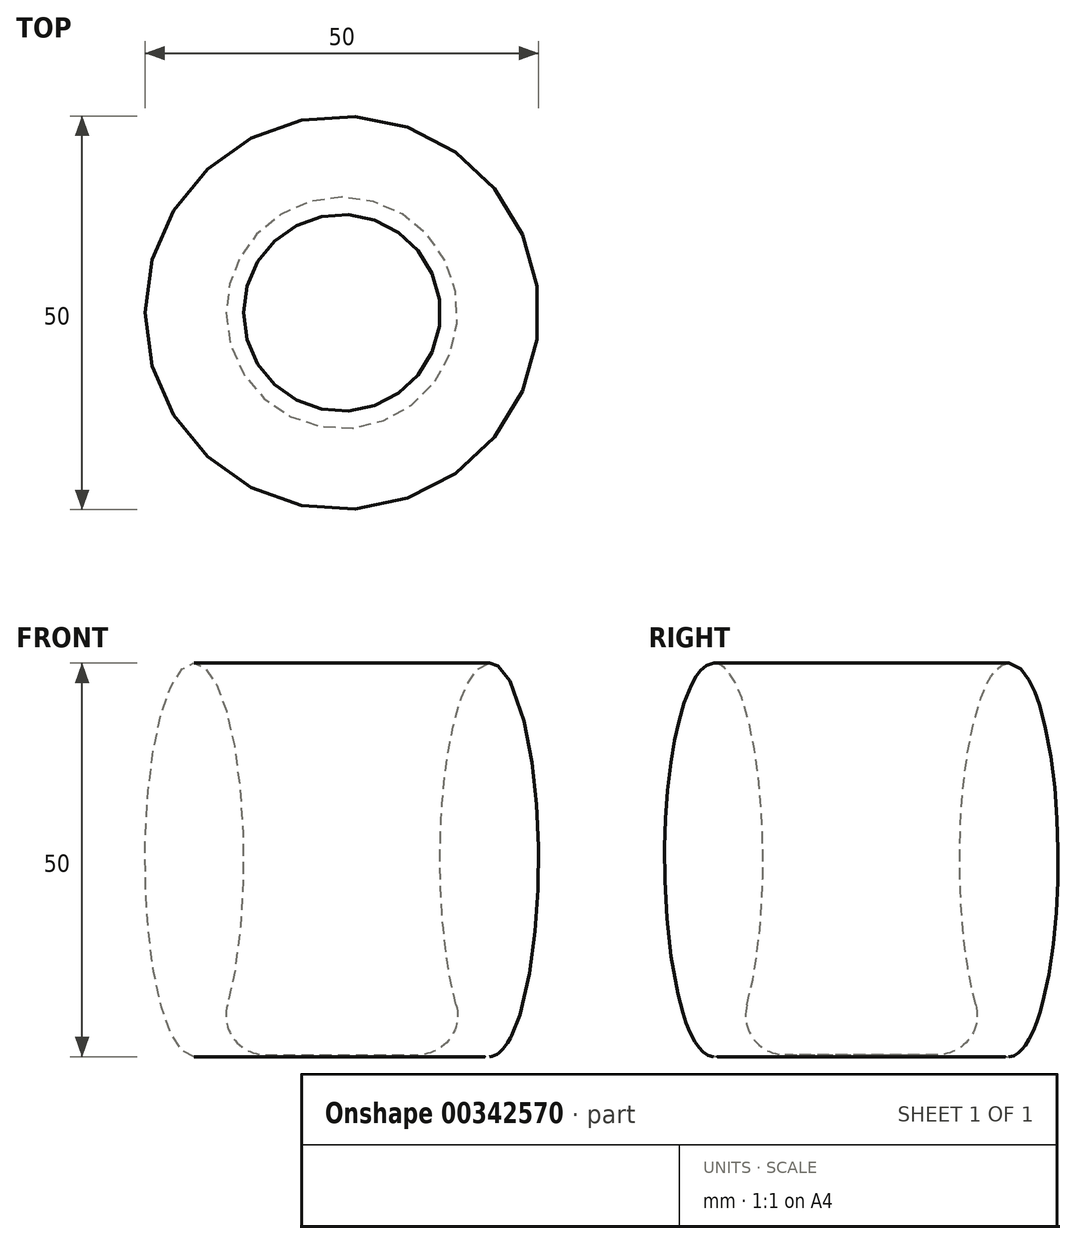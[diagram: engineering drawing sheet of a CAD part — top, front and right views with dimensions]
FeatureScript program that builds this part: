
annotation { "Feature Type Name" : "Feature", "Feature Type Description" : "" }
export const myFeature = defineFeature(function(context is Context, id is Id, definition is map)
    precondition{}
    {
        {
            var Q0;
            Q0=qCreatedBy(makeId("Front.planeOp"),FACE);
            var sketch = newSketch(context, id + "F0", { "sketchPlane" : qUnion([Q0])});
            skEllipticalArc(sketch, "E0", {});
            skLineSegment(sketch, "E1", {"start": v(0, 0) * mm, "end": v(0, 50) * mm, "construction": true});
            skPoint(sketch, "E2", {"position": v(12.5, 25) * mm});
            skPoint(sketch, "E3", {"position": v(25, 25) * mm});
            skLineSegment(sketch, "E4", {"start": v(18.75, 0) * mm, "end": v(0, 0) * mm});
            skLineSegment(sketch, "E5", {"start": v(0, 0) * mm, "end": v(0, 0.25) * mm});
            skLineSegment(sketch, "E6", {"start": v(0, 0.25) * mm, "end": v(9.7, 0.25) * mm});
            skPoint(sketch, "E7.orphan", {"position": v(18.75, 0.25) * mm});
            skPoint(sketch, "E8.visualSharp", {"position": v(17.87, 0.25) * mm});
            skArc(sketch, "E8.filletArc", {"start": v(9.7, 0.25) * mm, "mid": v(13.68, 2.22) * mm, "end": v(14.53, 6.57) * mm});
            const initialGuessF0  = {"E0": [0.01875, 0.025, 0, 1, 0.025, 0.00625, 3.141592653589793, 2.3999327056376534]};
            skSetInitialGuess(sketch, initialGuessF0);
            skSolve(sketch);
        }
        {
            var Q0;
            Q0=makeQuery(id+"F0.imprint","IMPRINT",FACE,{"disambiguationData":[TD([[makeQuery(id+"F0.imprint","IMPRINT",EDGE,{"derivedFrom":sQuery(id+"F0.wireOp",EDGE,"E0")}),1.0]])]});
            var Q1;
            Q1=makeQuery(id+"F0.imprint","IMPRINT",FACE,{"disambiguationData":[TD([[makeQuery(id+"F0.imprint","IMPRINT",EDGE,{"derivedFrom":sQuery(id+"F0.wireOp",EDGE,"793c75fe-19e5-4459-9b79-2bd3d177ff24.0")}),1.0]])]});
            var Q2;
            Q2=sQuery(id+"F0.wireOp",EDGE,"E1");
            revolve(context, id + "F1", {"entities" : qUnion([Q0, Q1]), "axis" : qUnion([Q2]), "revolveType" : RevolveType.FULL});
        }
    });
